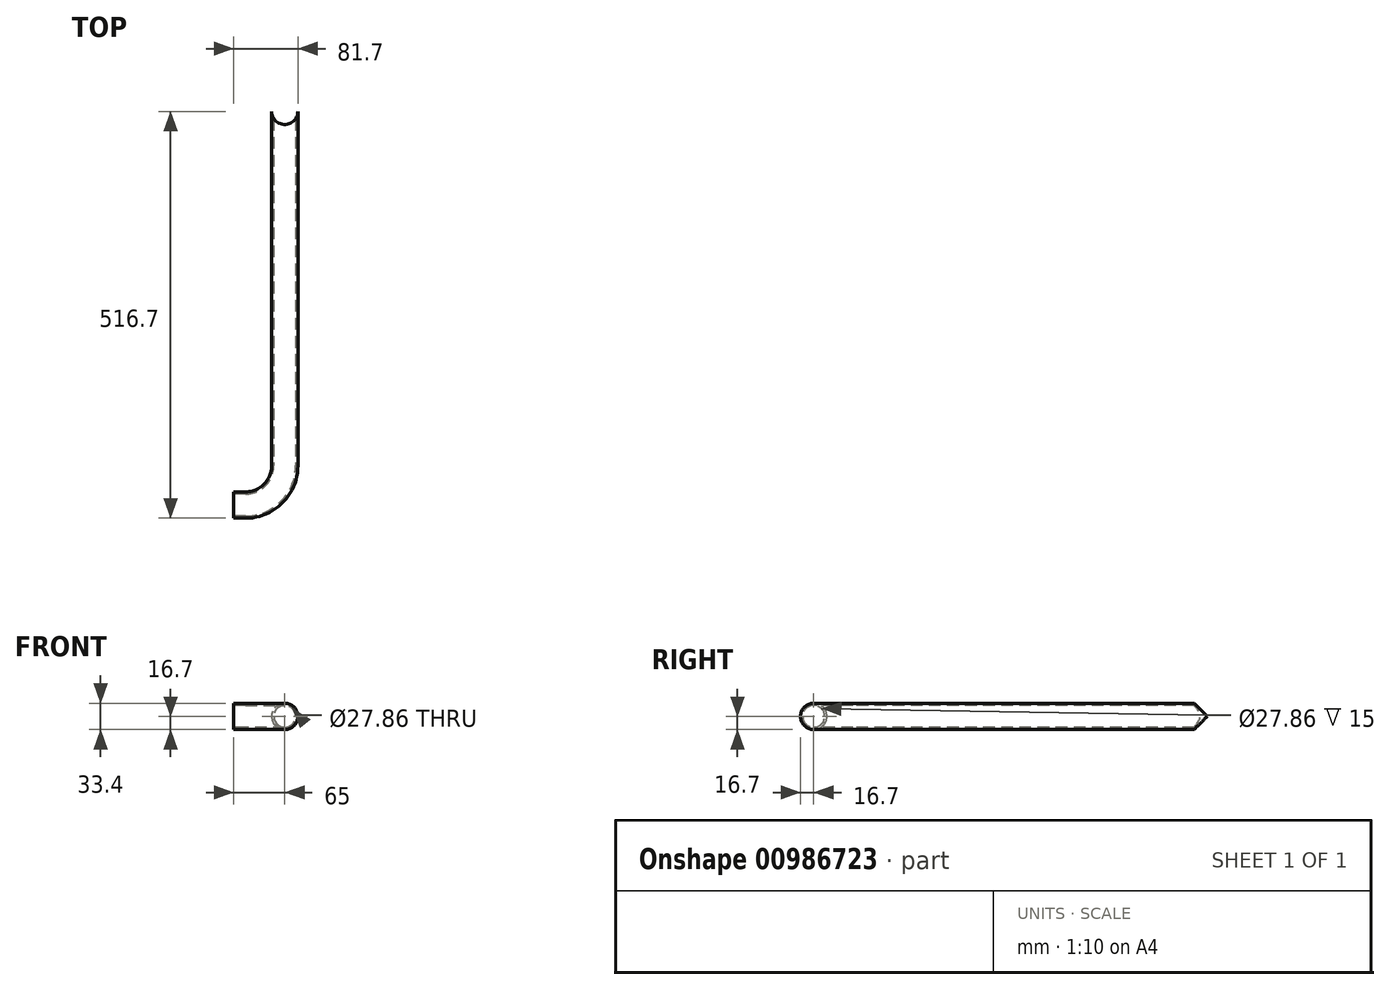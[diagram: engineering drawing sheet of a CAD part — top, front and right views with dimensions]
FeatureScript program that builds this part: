
annotation { "Feature Type Name" : "Feature", "Feature Type Description" : "" }
export const myFeature = defineFeature(function(context is Context, id is Id, definition is map)
    precondition{}
    {
        {
            var Q0;
            Q0=qCreatedBy(makeId("Top.planeOp"),FACE);
            var sketch = newSketch(context, id + "F0", { "sketchPlane" : qUnion([Q0])});
            skLineSegment(sketch, "E0", {"start": v(0, 0) * mm, "end": v(0, -450) * mm});
            skLineSegment(sketch, "E1", {"start": v(-50, -500) * mm, "end": v(-65, -500) * mm});
            skPoint(sketch, "E2.visualSharp", {"position": v(0, -500) * mm});
            skArc(sketch, "E2.filletArc", {"start": v(-50, -500) * mm, "mid": v(-14.64, -485.36) * mm, "end": v(0, -450) * mm});
            skSolve(sketch);
        }
        {
            var Q0;
            Q0=qCreatedBy(makeId("Front.planeOp"),FACE);
            var sketch = newSketch(context, id + "F1", { "sketchPlane" : qUnion([Q0])});
            skCircle(sketch, "E3", {"center": v(0, 0) * mm, "radius": 16.7 * mm});
            skCircle(sketch, "E4.0", {"center": v(0, 0) * mm, "radius": 13.93 * mm});
            skSolve(sketch);
        }
        {
            var Q0;
            Q0=makeQuery(id+"F1.imprint","IMPRINT",FACE,{"disambiguationData":[TD([[makeQuery(id+"F1.imprint","IMPRINT",EDGE,{"derivedFrom":sQuery(id+"F1.wireOp",EDGE,"E3")}),1.0]])]});
            var Q1;
            Q1=sQuery(id+"F0.wireOp",EDGE,"E0");
            var Q2;
            Q2=sQuery(id+"F0.wireOp",EDGE,"E2.filletArc");
            var Q3;
            Q3=sQuery(id+"F0.wireOp",EDGE,"E1");
            sweep(context, id + "F2", {"profiles" : qUnion([Q0]), "path" : qUnion([Q1, Q2, Q3])});
        }
        {
            var Q0;
            Q0=qCreatedBy(makeId("Top.planeOp"),FACE);
            var sketch = newSketch(context, id + "F3", { "sketchPlane" : qUnion([Q0])});
            skCircle(sketch, "E5", {"center": v(0, 0) * mm, "radius": 16.7 * mm});
            skSolve(sketch);
        }
        {
            var Q0;
            Q0 = qSketchRegion(id + "F3", true);
            extrude(context, id + "F4", {"entities" : qUnion([Q0]), "operationType" : NewBodyOperationType.REMOVE, "oppositeDirection" : true, "depth" : 25 * mm, "offsetDistance" : 25 * mm, "hasSecondDirection" : true, "secondDirectionOppositeDirection" : false, "secondDirectionDepth" : 25 * mm});
        }
    });
